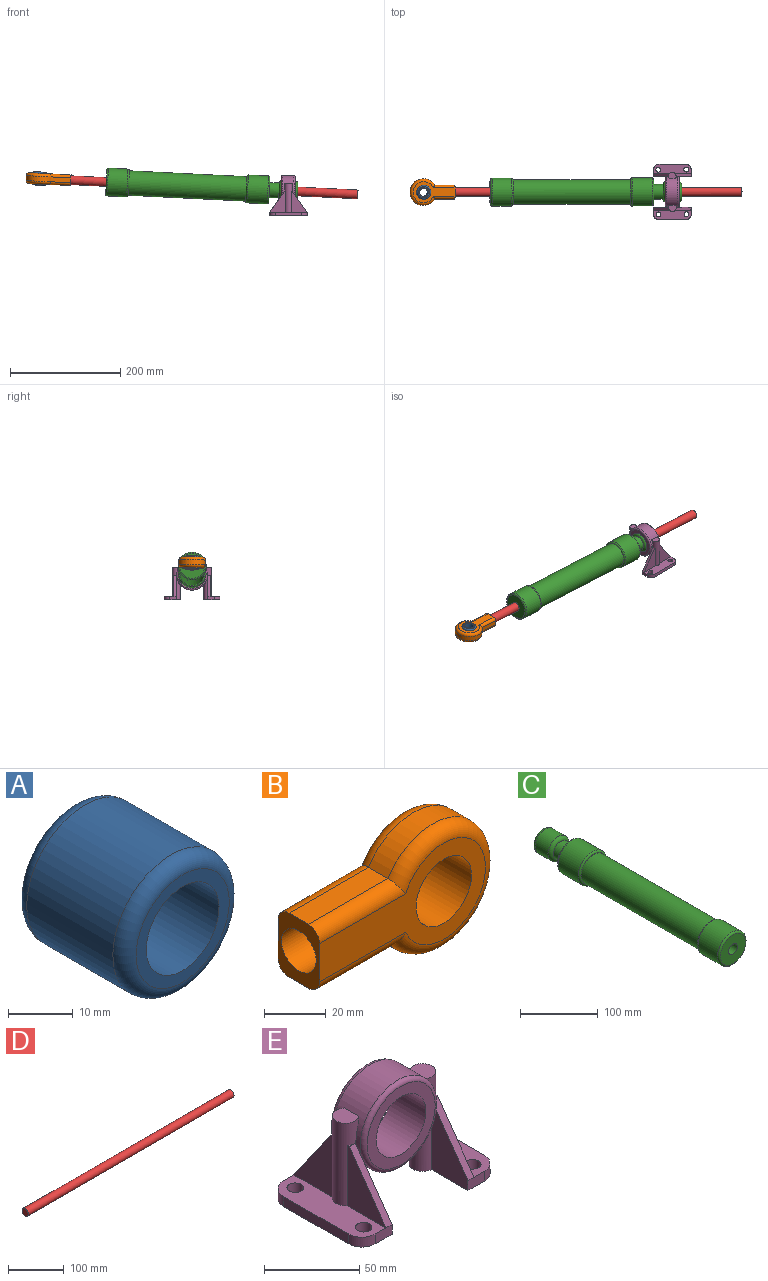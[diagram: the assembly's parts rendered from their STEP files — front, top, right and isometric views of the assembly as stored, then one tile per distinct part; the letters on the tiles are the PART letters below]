
ASSEMBLY  parts=5 mates=4
PART A: 6 faces, bbox 27.5x23.9x27.5 mm
  f0: cylinder r=12.7mm len=25.4mm, axis (0,1,0), area 1499.9mm2, adj f4,f5
  f1: plane 20.32x20.32mm, normal (0,-1,0), area 126.4mm2, adj f3,f5
  f2: plane 20.32x20.32mm, normal (0,1,0), area 126.4mm2, adj f3,f4
  f3: cylinder r=7.94mm len=23.88mm, axis (0,-1,0), area 1190.8mm2, adj f1,f2
  f4: torus R=10.16mm, axis (0,-1,0), area 295.2mm2, adj f0,f2
  f5: torus R=10.16mm, axis (0,-1,0), area 295.2mm2, adj f0,f1
PART B: 15 faces, bbox 83x19.1x52.2 mm
  f0: cylinder r=24.13mm len=48.26mm, axis (0,1,0), area 1110mm2, adj f3,f5,f8,f11
  f1: plane 75.89x38.1mm, normal (0,-1,0), area 1217.2mm2, adj f4,f6,f7,f8,f9
  f2: plane 75.89x38.1mm, normal (0,1,0), area 1217.2mm2, adj f4,f6,f10,f11,f12
  f3: plane 36.32x8.89mm, normal (0,0,1), area 322.9mm2, adj f0,f4,f9,f12
  f4: plane 25.4x19.05mm, normal (-1,0,0), area 263.8mm2, adj f1,f2,f3,f5,f7,f9,f10,f12
  f5: plane 36.32x8.89mm, normal (0,0,-1), area 322.9mm2, adj f0,f4,f7,f10
  f6: cylinder r=12.7mm len=25.4mm, axis (0,-1,0), area 1520.1mm2, adj f1,f2
  f7: cylinder r=5.08mm len=39.38mm, axis (-1,0,0), area 298.4mm2, adj f1,f4,f5,f8
  f8: torus R=19.05mm, axis (0,-1,0), area 936.2mm2, adj f0,f1,f7,f9
  f9: cylinder r=5.08mm len=39.38mm, axis (1,0,0), area 298.4mm2, adj f1,f3,f4,f8
  f10: cylinder r=5.08mm len=39.38mm, axis (1,0,0), area 298.4mm2, adj f2,f4,f5,f11
  f11: torus R=19.05mm, axis (0,-1,0), area 936.2mm2, adj f0,f2,f10,f12
  f12: cylinder r=5.08mm len=39.38mm, axis (-1,0,0), area 298.4mm2, adj f2,f3,f4,f11
  f13: cone r=0mm half-angle=59deg, axis (-1,0,0), area 230.9mm2, adj f14
  f14: cylinder r=7.94mm len=19.05mm, axis (-1,0,0), area 950.1mm2, adj f4,f13
PART C: 17 faces, bbox 55x347x55 mm
  f0: cylinder r=18.41mm len=36.83mm, axis (0,1,0), area 2704.5mm2, adj f7,f16
  f1: plane 26.67x26.67mm, normal (0,1,0), area 360.7mm2, adj f15,f16
  f2: cylinder r=13.59mm len=27.18mm, axis (0,1,0), area 1518.1mm2, adj f5,f7
  f3: cylinder r=25.4mm len=50.8mm, axis (0,1,0), area 5837.3mm2, adj f13,f14
  f4: plane 45.72x45.72mm, normal (0,-1,0), area 89.9mm2, adj f6,f14
  f5: plane 45.72x45.72mm, normal (0,1,0), area 1061.6mm2, adj f2,f13
  f6: cylinder r=22.23mm len=213.36mm, axis (0,1,0), area 29794.4mm2, adj f4,f10
  f7: torus R=13.33mm, axis (0,-1,0), area 809.2mm2, adj f0,f2
  f8: cylinder r=25.33mm len=50.65mm, axis (0,1,0), area 5658.7mm2, adj f11,f12
  f9: plane 45.57x45.57mm, normal (0,-1,0), area 1433.2mm2, adj f12,f15
  f10: plane 45.57x45.57mm, normal (0,1,0), area 79.4mm2, adj f6,f11
  f11: torus R=22.79mm, axis (0,-1,0), area 611.8mm2, adj f8,f10
  f12: torus R=22.79mm, axis (0,-1,0), area 611.8mm2, adj f8,f9
  f13: torus R=22.86mm, axis (0,-1,0), area 613.6mm2, adj f3,f5
  f14: torus R=22.86mm, axis (0,-1,0), area 613.6mm2, adj f3,f4
  f15: cylinder r=7.94mm len=346.96mm, axis (0,-1,0), area 17304.1mm2, adj f1,f9
  f16: torus R=13.33mm, axis (0,-1,0), area 830.7mm2, adj f0,f1
PART D: 3 faces, bbox 520.7x15.9x15.9 mm
  f0: cylinder r=7.94mm len=520.7mm, axis (-1,0,0), area 25968.8mm2, adj f1,f2
  f1: plane 15.88x15.88mm, normal (1,0,0), area 197.9mm2, adj f0
  f2: plane 15.88x15.88mm, normal (-1,0,0), area 197.9mm2, adj f0
PART E: 48 faces, bbox 101x68.3x75.3 mm
  f0: cylinder r=27.81mm len=55.63mm, axis (0,1,0), area 2701.8mm2, adj f1,f6,f7,f8,f25,f27
  f1: cylinder r=6.99mm len=59.44mm, axis (0,0,-1), area 1544.9mm2, adj f0,f2,f8,f9,f10,f11,f17,f18
  f2: plane 68.33x17.78mm, normal (0,0,1), area 1030.6mm2, adj f1,f12,f13,f14,f15,f16,f17,f22
  f3: plane 50.55x50.55mm, normal (0,-1,0), area 941.3mm2, adj f5,f7
  f4: plane 50.55x50.55mm, normal (0,1,0), area 941.3mm2, adj f5,f6
  f5: cylinder r=18.41mm len=36.83mm, axis (0,-1,0), area 2938.9mm2, adj f3,f4
  f6: torus R=25.27mm, axis (0,-1,0), area 674.1mm2, adj f0,f4
  f7: torus R=25.27mm, axis (0,-1,0), area 674.1mm2, adj f0,f3
  f8: plane 13.97x11.53mm, normal (0,0,1), area 135.3mm2, adj f0,f1
  f9: plane 68.33x29.06mm, normal (0,0,-1), area 1436.4mm2, adj f1,f10,f11,f12,f13,f14,f15,f16
  f10: plane 45.07x27.18mm, normal (1,0,0), area 699mm2, adj f1,f9,f14,f21,f24
  f11: plane 45.07x27.18mm, normal (1,0,0), area 699mm2, adj f1,f9,f12,f19,f20
  f12: plane 12.19x6.35mm, normal (0,1,0), area 77.4mm2, adj f2,f9,f11,f20,f46
  f13: plane 48.01x6.35mm, normal (-1,0,0), area 304.8mm2, adj f2,f9,f46,f47
  f14: plane 12.19x6.35mm, normal (0,-1,0), area 77.4mm2, adj f2,f9,f10,f24,f47
  f15: cylinder r=4.36mm len=8.71mm, axis (0,0,1), area 173.8mm2, adj f2,f9
  f16: cylinder r=4.36mm len=8.71mm, axis (0,0,1), area 173.8mm2, adj f2,f9
  f17: plane 38.72x28.65mm, normal (-1,0,0), area 583.3mm2, adj f1,f2,f18,f20
  f18: plane 4.29x1.47mm, normal (0,0,1), area 2mm2, adj f1,f17,f20
  f19: plane 0.28x0.01mm, normal (0,0,1), area 0mm2, adj f1,f11,f20
  f20: plane 38.72x27.18mm, normal (0,0.82,0.57), area 216.3mm2, adj f11,f12,f17,f18,f19
  f21: plane 0.28x0.01mm, normal (0,0,1), area 0mm2, adj f1,f10,f24
  f22: plane 38.72x28.65mm, normal (-1,0,0), area 583.3mm2, adj f1,f2,f23,f24
  f23: plane 4.29x1.47mm, normal (0,0,1), area 2mm2, adj f1,f22,f24
  f24: plane 38.72x27.18mm, normal (0,-0.82,0.57), area 216.3mm2, adj f10,f14,f21,f22,f23
  f25: cylinder r=6.99mm len=59.44mm, axis (0,0,-1), area 1545mm2, adj f0,f26,f27,f28,f29,f30,f36,f37
  f26: plane 68.33x17.78mm, normal (0,0,1), area 1030.6mm2, adj f25,f31,f32,f33,f34,f35,f36,f41
  f27: plane 13.97x11.53mm, normal (0,0,1), area 135.3mm2, adj f0,f25
  f28: plane 68.33x29.06mm, normal (0,0,-1), area 1436.4mm2, adj f25,f29,f30,f31,f32,f33,f34,f35
  f29: plane 45.07x27.18mm, normal (-1,0,0), area 699mm2, adj f25,f28,f33,f40,f43
  f30: plane 45.07x27.18mm, normal (-1,0,0), area 699mm2, adj f25,f28,f31,f38,f39
  f31: plane 12.19x6.35mm, normal (0,1,0), area 77.4mm2, adj f26,f28,f30,f39,f44
  f32: plane 48.01x6.35mm, normal (1,0,0), area 304.8mm2, adj f26,f28,f44,f45
  f33: plane 12.19x6.35mm, normal (0,-1,0), area 77.4mm2, adj f26,f28,f29,f43,f45
  f34: cylinder r=4.36mm len=8.71mm, axis (0,0,1), area 173.8mm2, adj f26,f28
  f35: cylinder r=4.36mm len=8.71mm, axis (0,0,1), area 173.8mm2, adj f26,f28
  f36: plane 38.72x28.65mm, normal (1,0,0), area 583.3mm2, adj f25,f26,f37,f39
  f37: plane 4.29x1.47mm, normal (0,0,1), area 2mm2, adj f25,f36,f39
  f38: plane 0.28x0.01mm, normal (0,0,1), area 0mm2, adj f25,f30,f39
  f39: plane 38.72x27.18mm, normal (0,0.82,0.57), area 216.3mm2, adj f30,f31,f36,f37,f38
  f40: plane 0.28x0.01mm, normal (0,0,1), area 0mm2, adj f25,f29,f43
  f41: plane 38.72x28.65mm, normal (1,0,0), area 583.3mm2, adj f25,f26,f42,f43
  f42: plane 4.29x1.47mm, normal (0,0,1), area 2mm2, adj f25,f41,f43
  f43: plane 38.72x27.18mm, normal (0,-0.82,0.57), area 216.3mm2, adj f29,f33,f40,f41,f42
  f44: cylinder r=10.16mm len=10.16mm, axis (0,0,1), area 101.3mm2, adj f26,f28,f31,f32
  f45: cylinder r=10.16mm len=10.16mm, axis (0,0,-1), area 101.3mm2, adj f26,f28,f32,f33
  f46: cylinder r=10.16mm len=10.16mm, axis (0,0,1), area 101.3mm2, adj f2,f9,f12,f13
  f47: cylinder r=10.16mm len=10.16mm, axis (0,0,-1), area 101.3mm2, adj f2,f9,f13,f14
PLACE A rot(axis=(-0.96,-0.17,0.25),90deg) t=(-171.02,-334.4,71.48)mm
PLACE B rot(axis=(0.02,-0.71,0.7),178deg) t=(-173.01,-287.45,75.4)mm
PLACE C rot(axis=(0.01,0.05,-1),90.1deg) t=(295.23,-287.22,61.76)mm
PLACE D rot(axis=(0.77,0.64,-0.01),4.4deg) t=(-115.77,-287.54,82.1)mm
PLACE E rot(axis=(0,0,-1),89.8deg) t=(278.48,-287.24,62.59)mm
MATE ball B.f0 <-> A.f0  axis (0.05,-0.01,1) through (-172.54,-287.59,84.91)mm
MATE ball C.f0 <-> E.f0  axis (1,0,-0.05) through (278.48,-287.24,62.59)mm
MATE cylindrical C.f0 <-> D.f0  axis (1,0,-0.05) through (295.23,-287.22,61.76)mm
MATE revolute B.f13 <-> D.f0  axis (1,0,-0.05) through (-115.77,-287.54,82.1)mm
